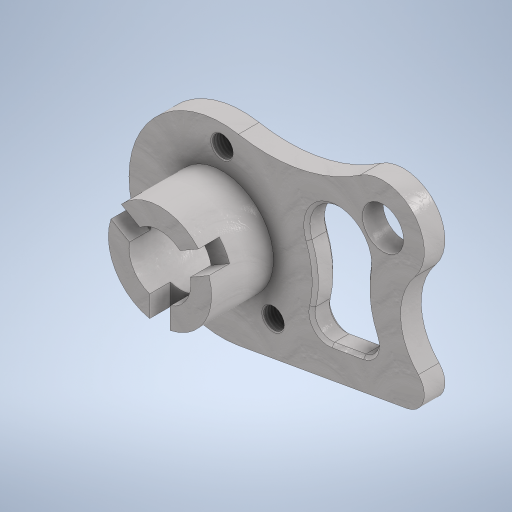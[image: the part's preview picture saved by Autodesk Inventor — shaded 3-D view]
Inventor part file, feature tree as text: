
AUTODESK INVENTOR PART (.ipt)
format: ipt  version: 2023 (Build 270158030, 158C)  size: 449,536 bytes
history: native  units: mm
features: extrude x4, sketch x4, chamfer x3, thread x3
ambient origin geometry x8: Origin, YZ Plane, XZ Plane, XY Plane, X Axis, Y Axis, Z Axis, Center Point
bodies: Solid1 (feature_tree)
feature tree (14):
  extrude  "Extrusion1"  Depth=40.0mm
  extrude  "Extrusion2"  Depth=78.0mm
  chamfer  "Chamfer1"  Distance=20.0mm
  chamfer  "Chamfer2"  Distance=60.0mm
  extrude  "Extrusion3"  Depth=10.0mm
  extrude  "Extrusion4"  Depth=10.0mm
  thread  "Thread1"  [1 undecoded]
  thread  "Thread2"  [1 undecoded]
  thread  "Thread3"  [1 undecoded]
  chamfer  "Chamfer4"  Distance=15.5mm
  sketch  "Sketch1"  dims[d1=160.0mm d2=40.0mm]
  sketch  "Sketch2"  dims[d3=40.0mm d4=78.0mm]
  sketch  "Sketch3"  dims[d6=20.0mm]
  sketch  "Sketch4"  dims[d7=88.0mm d8=20.0mm d9=60.0mm d10=20.0mm d11=90.0mm d12=30.0mm d13=22.0mm d22=16.0mm d23=15.5mm d26=90.0mm d29=10.0mm d32=10.0mm d33=10.0mm d34=10.0mm d35=0.0mm d36=50.0mm d37=30.0mm d54=150.0deg d59=10.0mm d61=30.0mm d62=0.0mm d63=0.5mm d64=2.0mm d65=45.0deg d66=1.5mm d67=2.0mm d68=45.0deg d72=20.0mm d73=0.0mm d74=10.0mm d75=0.0mm d76=15.0mm d77=23.2mm d78=0.0mm d79=23.2mm d80=0.0mm d81=23.2mm d82=0.0mm d86=1.5mm d87=2.0mm d88=45.0deg d83=0.0625mm d84=0.75mm d85=0.375mm]
note: 3 required parameter values undecoded (feature->parameter linkage not recoverable at this tier; creation-order binding heuristic only, values carry confidence <= 0.55)
